FCSTD DOCUMENT  (FreeCAD 1.0R39319 (Git))
Label: Week1Assignment2
License: All rights reserved
LicenseURL: https://en.wikipedia.org/wiki/All_rights_reserved
objects: Sketcher::SketchObject×1
note: 2 computed .brp shape members not serialized (recipe doc carries the construction recipe); baked Part::Feature solids carry a one-line shape summary decoded from their .brp

FEATURE [Sketcher::SketchObject] Sketch
  ArcFitTolerance = 1e-06
  FullyConstrained = true
  MakeInternals = false
  sketch-geometry (16):
    g0: Circle CenterX=28.3642 CenterY=122.138 CenterZ=0 NormalX=0 NormalY=0 NormalZ=1 AngleXU=0 Radius=7.5
    g1: ArcOfCircle CenterX=28.3642 CenterY=122.138 CenterZ=0 NormalX=0 NormalY=0 NormalZ=1 AngleXU=0 Radius=15 StartAngle=1.66917 EndAngle=3.14159
    g2: LineSegment [constr] StartX=28.3642 StartY=122.138 StartZ=0 EndX=28.3642 EndY=52.1377 EndZ=0
    g3: LineSegment [constr] StartX=28.3642 StartY=52.1377 StartZ=0 EndX=88.3642 EndY=52.1377 EndZ=0
    g4: LineSegment [constr] StartX=88.3642 StartY=52.1377 StartZ=0 EndX=88.3642 EndY=122.138 EndZ=0
    g5: LineSegment [constr] StartX=88.3642 StartY=122.138 StartZ=0 EndX=28.3642 EndY=122.138 EndZ=0
    g6: Circle CenterX=88.3642 CenterY=52.1377 CenterZ=0 NormalX=0 NormalY=0 NormalZ=1 AngleXU=0 Radius=7.5
    g7: ArcOfCircle CenterX=88.3642 CenterY=52.1377 CenterZ=0 NormalX=0 NormalY=0 NormalZ=1 AngleXU=0 Radius=20 StartAngle=4.71239 EndAngle=8.43559
    g8: LineSegment StartX=13.3642 StartY=122.138 StartZ=0 EndX=13.3642 EndY=92.1377 EndZ=0
    g9: ArcOfCircle CenterX=23.3642 CenterY=92.1377 CenterZ=0 NormalX=0 NormalY=0 NormalZ=1 AngleXU=0 Radius=10 StartAngle=3.14159 EndAngle=4.71239
    g10: LineSegment StartX=23.3642 StartY=82.1377 StartZ=0 EndX=33.3642 EndY=82.1377 EndZ=0
    g11: ArcOfCircle CenterX=33.3642 CenterY=72.1377 CenterZ=0 NormalX=0 NormalY=0 NormalZ=1 AngleXU=0 Radius=10 StartAngle=6.28318 EndAngle=7.85398
    g12: LineSegment StartX=43.3642 StartY=72.1377 StartZ=0 EndX=43.3642 EndY=62.1377 EndZ=0
    g13: ArcOfCircle CenterX=73.3642 CenterY=62.1377 CenterZ=0 NormalX=0 NormalY=0 NormalZ=1 AngleXU=0 Radius=30 StartAngle=3.14159 EndAngle=4.71239
    g14: LineSegment StartX=73.3642 StartY=32.1377 StartZ=0 EndX=88.3642 EndY=32.1377 EndZ=0
    g15: ArcOfCircle CenterX=31.7463 CenterY=87.8686 CenterZ=0 NormalX=0 NormalY=0 NormalZ=1 AngleXU=0 Radius=49.4357 StartAngle=5.88827 EndAngle=7.95235
  constraints (40):
    c: Diameter(g0) = 15
    c: Diameter(g1) = 30
    c: Coincident(g1,g0)
    c: Coincident(g2,g3)
    c: Coincident(g3,g4)
    c: Coincident(g4,g5)
    c: Coincident(g5,g2)
    c: Vertical(g2)
    c: Vertical(g4)
    c: Horizontal(g3)
    c: Horizontal(g5)
    c: Distance(g2,g4) = 60
    c: Distance(g3,g5) = 70
    c: Coincident(g2,g0)
    c: Diameter(g6) = 15
    c: Coincident(g6,g3)
    c: Diameter(g7) = 40
    c: Coincident(g7,g3)
    c: Vertical(g8)
    c: Tangent(g8,g9) = -1.5708
    c: Horizontal(g10)
    c: Tangent(g10,g11) = 1.5708
    c: Coincident(g11,g12)
    c: Vertical(g12)
    c: Tangent(g12,g13) = -1.5708
    c: Radius(g9) = 10
    c: DistanceX(g10,g10) = 10
    c: Radius(g11) = 10
    c: Radius(g13) = 30
    c: Tangent(g13,g14) = -1.5708
    c: Horizontal(g14)
    c: Distance(g5,g10) = 40
    c: Tangent(g9,g10) = -1.5708
    c: Distance(g4,g12) = 45
    c: Coincident(g7,g15)
    c: Tangent(g7,g14) = -1.5708
    c: Tangent(g1,g15) = -1.5708
    c: Tangent(g1,g8) = -1.5708
    c: Block(g1)
    c: Block(g15)
